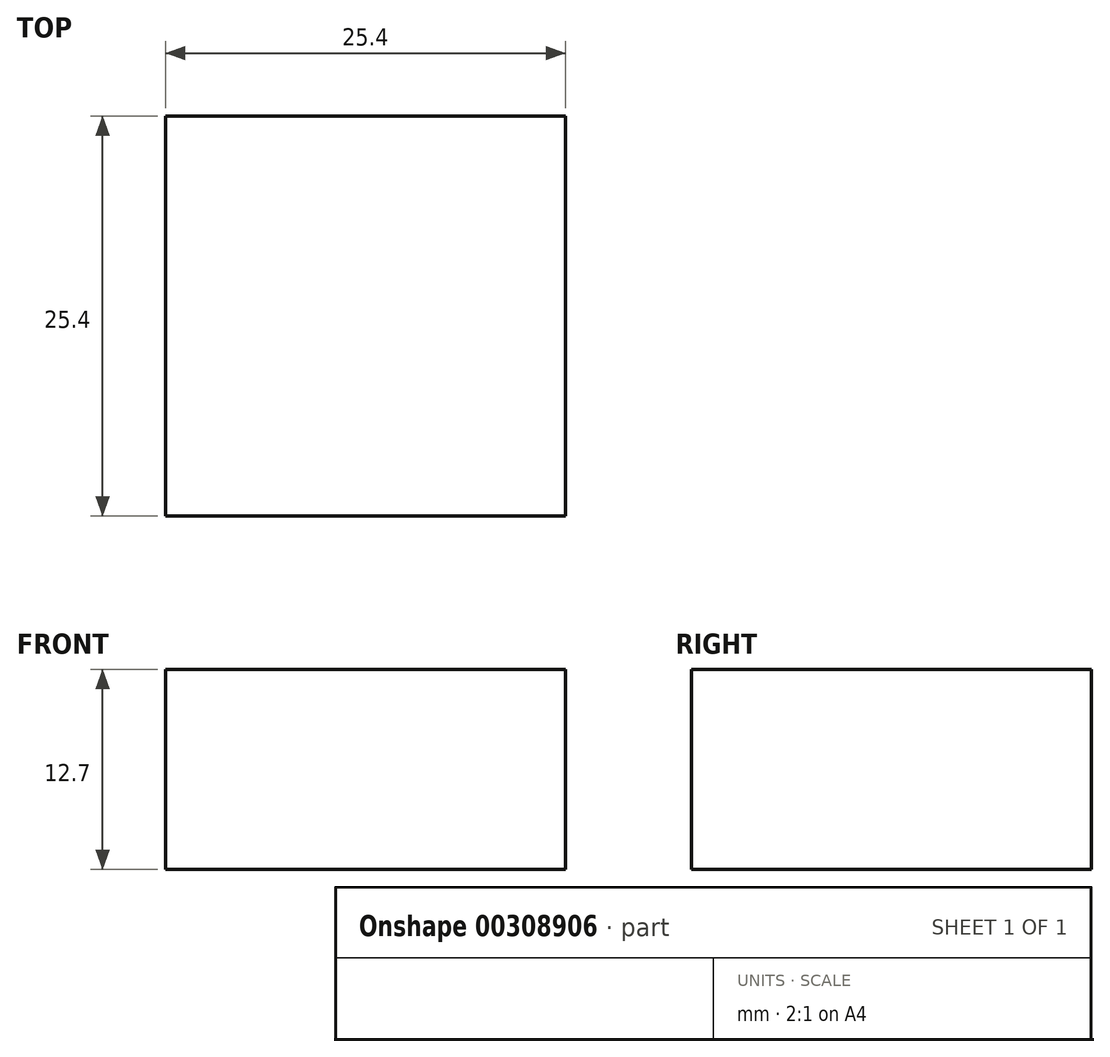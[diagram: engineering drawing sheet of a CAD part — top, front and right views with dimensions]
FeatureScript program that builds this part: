
annotation { "Feature Type Name" : "Feature", "Feature Type Description" : "" }
export const myFeature = defineFeature(function(context is Context, id is Id, definition is map)
    precondition{}
    {
        {
            var Q0;
            Q0=qCreatedBy(makeId("Front.planeOp"),FACE);
            var sketch = newSketch(context, id + "F0", { "sketchPlane" : qUnion([Q0])});
            skLineSegment(sketch, "E0.bottom", {"start": v(12.7, -6.35) * mm, "end": v(-12.7, -6.35) * mm});
            skLineSegment(sketch, "E0.top", {"start": v(12.7, 6.35) * mm, "end": v(-12.7, 6.35) * mm});
            skLineSegment(sketch, "E0.left", {"start": v(12.7, -6.35) * mm, "end": v(12.7, 6.35) * mm});
            skLineSegment(sketch, "E0.right", {"start": v(-12.7, -6.35) * mm, "end": v(-12.7, 6.35) * mm});
            skPoint(sketch, "E0.middle", {"position": v(0, 0) * mm});
            skSolve(sketch);
        }
        {
            var Q0;
            Q0=makeQuery(id+"F0.imprint","IMPRINT",FACE,{"disambiguationData":[TD([[makeQuery(id+"F0.imprint","IMPRINT",EDGE,{"derivedFrom":sQuery(id+"F0.wireOp",EDGE,"E0.bottom")}),-1.0]])]});
            extrude(context, id + "F1", {"entities" : qUnion([Q0]), "endBound" : BoundingType.SYMMETRIC, "depth" : 25.4 * mm});
        }
    });
